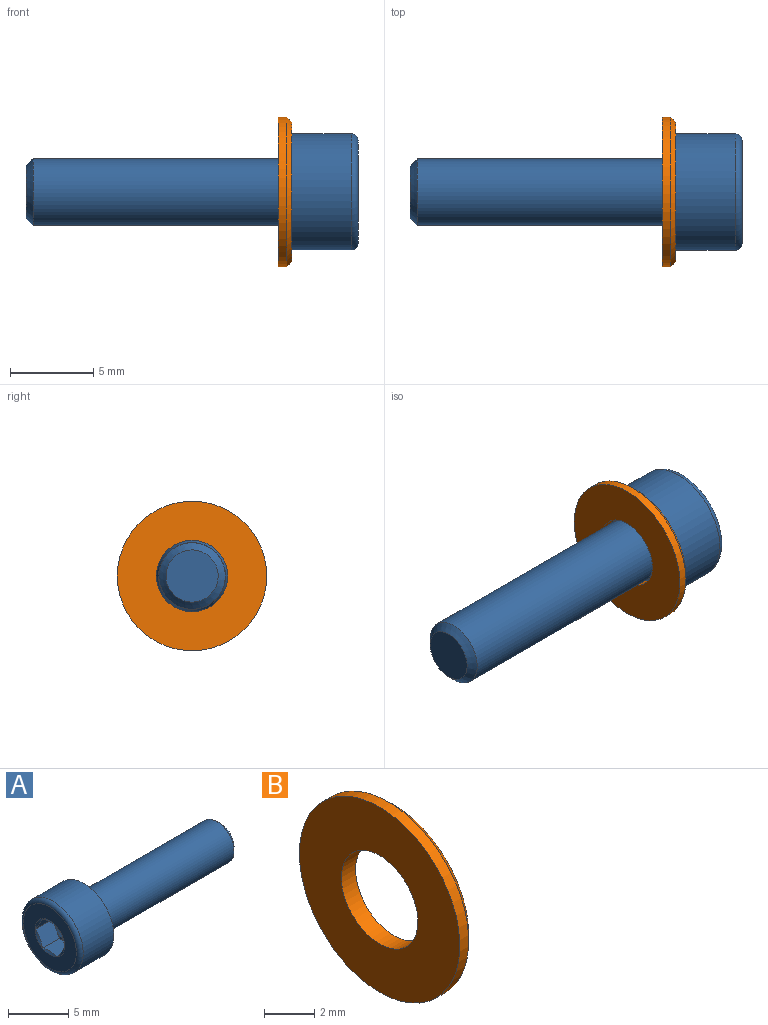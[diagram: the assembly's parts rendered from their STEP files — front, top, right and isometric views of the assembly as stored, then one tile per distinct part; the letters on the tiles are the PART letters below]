
ASSEMBLY  parts=2 mates=1
PART A: 24 faces, bbox 20x7.6x7.6 mm
  f0: plane 1.3x0.75mm, normal (-1,0,0), area 0.1mm2, adj f16,f17,f23
  f1: plane 1.5x0.43mm, normal (-1,0,0), area 0.1mm2, adj f17,f18,f23
  f2: plane 1.3x0.75mm, normal (-1,0,0), area 0.1mm2, adj f18,f19,f23
  f3: plane 1.3x0.75mm, normal (-1,0,0), area 0.1mm2, adj f19,f20,f23
  f4: plane 1.5x0.43mm, normal (-1,0,0), area 0.1mm2, adj f20,f21,f23
  f5: cone r=1.74mm half-angle=60deg, axis (-1,0,0), area 2mm2, adj f15,f16,f17,f18,f19,f20,f21
  f6: cone r=2.01mm half-angle=20.6deg, axis (-1,0,0), area 5.6mm2, adj f7,f11
  f7: torus R=2.2mm, axis (1,0,0), area 0.9mm2, adj f6,f10
  f8: plane 3.14x3.14mm, normal (1,0,0), area 7.7mm2, adj f9
  f9: cone r=2mm half-angle=45deg, axis (-1,0,0), area 6.8mm2, adj f8,f10
  f10: cylinder r=2mm len=14.97mm, axis (1,0,0), area 188.1mm2, adj f7,f9
  f11: torus R=2.35mm, axis (1,0,0), area 3.4mm2, adj f6,f13
  f12: cylinder r=3.5mm len=7mm, axis (1,0,0), area 79.2mm2, adj f13,f14
  f13: plane 7x7mm, normal (1,0,0), area 21.1mm2, adj f11,f12
  f14: torus R=3.1mm, axis (1,0,0), area 13.2mm2, adj f12,f15
  f15: plane 6.2x6.2mm, normal (-1,0,0), area 20.7mm2, adj f5,f14
  f16: plane 2x1.74mm, normal (0,0,-1), area 3.3mm2, adj f0,f5,f17,f21,f22
  f17: plane 2x1.5mm, normal (0,0.87,-0.5), area 3.3mm2, adj f0,f1,f5,f16,f18
  f18: plane 2x1.5mm, normal (0,0.87,0.5), area 3.3mm2, adj f1,f2,f5,f17,f19
  f19: plane 2x1.74mm, normal (0,0,1), area 3.3mm2, adj f2,f3,f5,f18,f20
  f20: plane 2x1.5mm, normal (0,-0.87,0.5), area 3.3mm2, adj f3,f4,f5,f19,f21
  f21: plane 2x1.5mm, normal (0,-0.87,-0.5), area 3.3mm2, adj f4,f5,f16,f20,f22
  f22: plane 1.3x0.75mm, normal (-1,0,0), area 0.1mm2, adj f16,f21,f23
  f23: cone r=1.5mm half-angle=60deg, axis (-1,0,0), area 8.2mm2, adj f0,f1,f2,f3,f4,f22
PART B: 5 faces, bbox 0.8x9x9 mm
  f0: plane 9x9mm, normal (-1,0,0), area 49.1mm2, adj f1,f4
  f1: cylinder r=2.15mm len=4.3mm, axis (1,0,0), area 10.8mm2, adj f0,f2
  f2: plane 8.4x8.4mm, normal (1,0,0), area 40.9mm2, adj f1,f3
  f3: cone r=4.2mm half-angle=45deg, axis (-1,0,0), area 11.6mm2, adj f2,f4
  f4: cylinder r=4.5mm len=9mm, axis (1,0,0), area 14.1mm2, adj f0,f3
PLACE A rot(axis=(0,1,0),180deg) t=(0.8,0,0)mm
PLACE B at identity fixed
MATE fastened A.f5 <-> B.f1  axis (-1,0,0) through (0.8,0,0)mm
